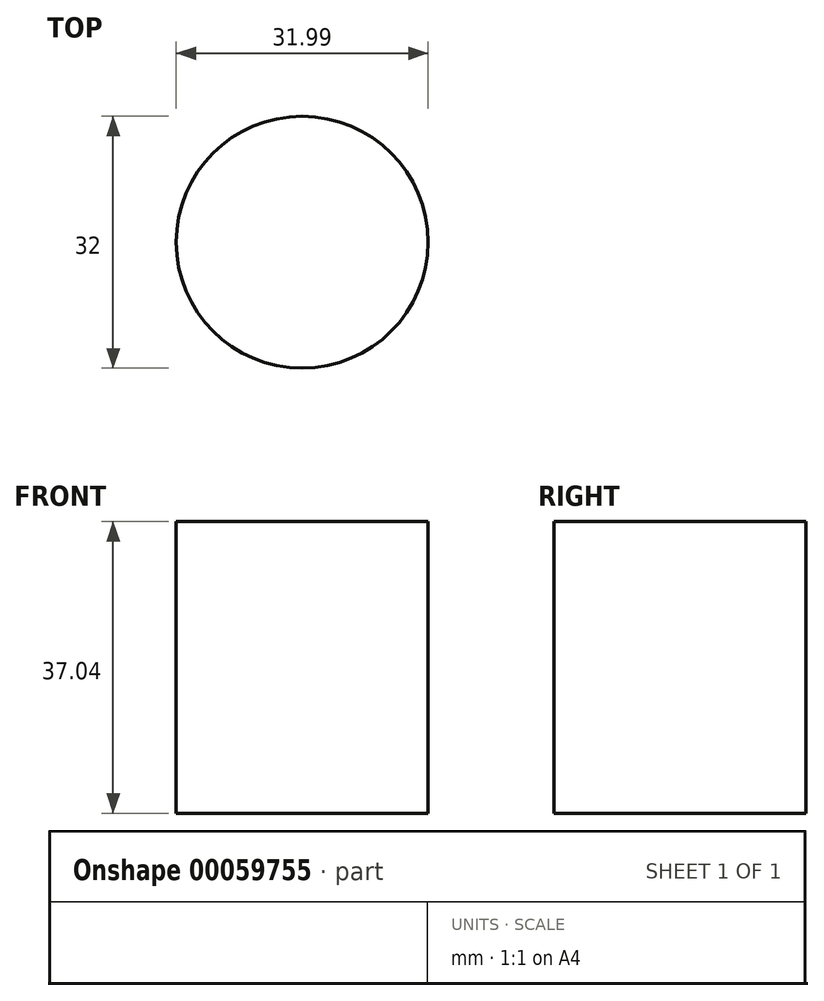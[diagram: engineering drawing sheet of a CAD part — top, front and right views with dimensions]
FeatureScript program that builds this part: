
annotation { "Feature Type Name" : "Feature", "Feature Type Description" : "" }
export const myFeature = defineFeature(function(context is Context, id is Id, definition is map)
    precondition{}
    {
        {
            var Q0;
            Q0=qCreatedBy(makeId("Top.planeOp"),FACE);
            var sketch = newSketch(context, id + "F0", { "sketchPlane" : qUnion([Q0])});
            skCircle(sketch, "E0", {"center": v(0, 0) * mm, "radius": 73.45 * mm});
            skCircle(sketch, "E1", {"center": v(0, 0) * mm, "radius": 16.64 * mm});
            skSolve(sketch);
        }
        {
            var Q0;
            Q0=makeQuery(id+"F0.imprint","IMPRINT",FACE,{"disambiguationData":[TD([[makeQuery(id+"F0.imprint","IMPRINT",EDGE,{"derivedFrom":sQuery(id+"F0.wireOp",EDGE,"E0")}),1.0]])]});
            extrude(context, id + "F1", {"entities" : qUnion([Q0]), "depth" : 37.04 * mm});
        }
        {
            var Q0;
            Q0=makeQuery(id+"F1.opExtrude","CAP_FACE",FACE,{"disambiguationData":[OSD([sQuery(id+"F0.wireOp",EDGE,"E0"),sQuery(id+"F0.wireOp",EDGE,"E1")])],"isStart":false});
            var sketch = newSketch(context, id + "F4", { "sketchPlane" : qUnion([Q0])});
            skCircle(sketch, "E2", {"center": v(31.04, 42.35) * mm, "radius": 16 * mm});
            skSolve(sketch);
        }
        {
            var Q0;
            Q0=makeQuery(id+"FAZTPMVeSh+oyARpN_1.boolean.opBoolean","COPY",FACE,{"derivedFrom":makeQuery(id+"FAZTPMVeSh+oyARpN_1.opExtrude","CAP_FACE",FACE,{"disambiguationData":[OSD([sQuery(id+"F4.wireOp",EDGE,"E2")])],"isStart":false})});
            var Q1;
            Q1=makeQuery(id+"F4.imprint","IMPRINT",FACE,{"disambiguationData":[TD([[makeQuery(id+"F4.imprint","IMPRINT",EDGE,{"derivedFrom":sQuery(id+"F4.wireOp",EDGE,"E2")}),-1.0]])]});
            extrude(context, id + "F2", {"entities" : qUnion([Q0, Q1]), "operationType" : NewBodyOperationType.REMOVE, "oppositeDirection" : true, "depth" : 50.8 * mm});
        }
    });
